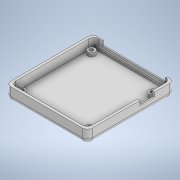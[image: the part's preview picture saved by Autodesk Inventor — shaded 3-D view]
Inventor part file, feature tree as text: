
AUTODESK INVENTOR PART (.ipt)
format: ipt  version: 2021 (Build 250183000, 183)  size: 407,552 bytes
history: native  units: mm
features: extrude x14, sketch x13, projected_geometry x3, fillet x1
ambient origin geometry x8: Origin, YZ Plane, XZ Plane, XY Plane, X Axis, Y Axis, Z Axis, Center Point
bodies: Solid1 (feature_tree)
feature tree (31):
  extrude  "Extrusion1"  Depth=62.0mm
  extrude  "Extrusion2"  Depth=3.0mm
  extrude  "Extrusion56"  Depth=3.0mm
  extrude  "Extrusion58"  Depth=3.0mm
  extrude  "Extrusion59"  Depth=3.0mm
  extrude  "Extrusion60"  Depth=54.35mm
  extrude  "Extrusion61"  Depth=51.56mm
  extrude  "Extrusion62"  Depth=6.0mm
  extrude  "Extrusion63"  Depth=6.0mm
  extrude  "Extrusion64"  Depth=20.0mm
  extrude  "Extrusion65"  Depth=1.0mm
  extrude  "Extrusion66"  Depth=3.0mm
  extrude  "Extrusion67"  Depth=3.0mm
  fillet  "Fillet13"  Radius=2.5mm
  extrude  "Extrusion68"  Depth=3.0mm
  sketch  "Sketch2"  dims[d14=66.0mm d15=62.0mm]
  sketch  "Sketch69"  dims[d16=3.0mm d17=3.0mm]
  sketch  "Sketch72"  dims[d18=3.0mm d19=3.0mm]
  sketch  "Sketch73"  dims[d20=3.0mm d21=4.5mm]
  sketch  "Sketch74"  dims[d22=6.0mm d23=3.0mm]
  sketch  "Sketch75"  dims[d24=57.4mm d25=54.35mm]
  sketch  "Sketch77"  dims[d26=0.8mm d27=51.56mm]
  sketch  "Sketch78"  dims[d28=4.8mm d29=6.0mm]
  projected_geometry  "Projected Loop3"
  projected_geometry  "Projected Loop4"
  sketch  "Sketch80"  dims[d30=6.0mm d31=6.0mm]
  sketch  "Sketch81"  dims[d32=20.0mm d33=20.0mm]
  sketch  "Sketch82"  dims[d34=1.0mm d35=1.0mm]
  projected_geometry  "Projected Loop5"
  sketch  "Sketch83"  dims[d36=2.0mm d37=0.0mm]
  sketch  "Sketch84"  dims[d38=66.0mm d40=3.0mm d41=3.0mm d42=3.0mm d43=3.0mm d44=3.0mm d45=4.5mm d46=6.0mm d47=3.0mm d48=57.4mm d50=0.8mm d51=51.56mm d52=4.8mm d53=6.0mm d54=6.0mm d55=6.0mm d62=3.0mm d63=0.0mm d181=2.0mm d182=2.0mm d184=2.0mm d186=2.0mm d187=8.0mm d190=8.0mm d193=8.0mm d196=8.0mm d432=2.5mm d433=2.5mm d434=2.5mm d435=2.5mm d436=3.0mm d437=0.0mm d446=6.0mm d447=0.0mm d448=6.0mm d449=7.0mm d450=7.1mm d451=2.0mm d452=0.0mm d453=2.0mm d454=6.0mm d455=0.0mm d457=52.5mm d458=1.0mm d459=4.3mm d460=12.0mm d461=3.0mm d462=0.0mm d463=3.0mm d464=0.0mm d465=0.0mm d466=1.5mm d467=0.0mm d469=1.0mm d470=1.5mm d471=0.0mm d472=2.0mm d473=0.0mm d475=4.0mm d476=10.0mm d477=0.0mm d478=4.0mm d479=10.0mm d480=0.0mm d482=1.0mm d483=0.0mm d484=3.0mm d486=3.0mm d487=3.0mm d488=3.0mm d489=1011.0mm d490=0.0mm d491=4.0mm d492=6.0mm d493=6.0mm d494=6.0mm d495=6.0mm d496=2.5mm d497=0.0mm d409=0.5mm d410=0.872665mm d411=0.5mm d412=0.872665mm d417=0.5mm d418=0.872665mm d419=0.5mm d420=0.872665mm]
